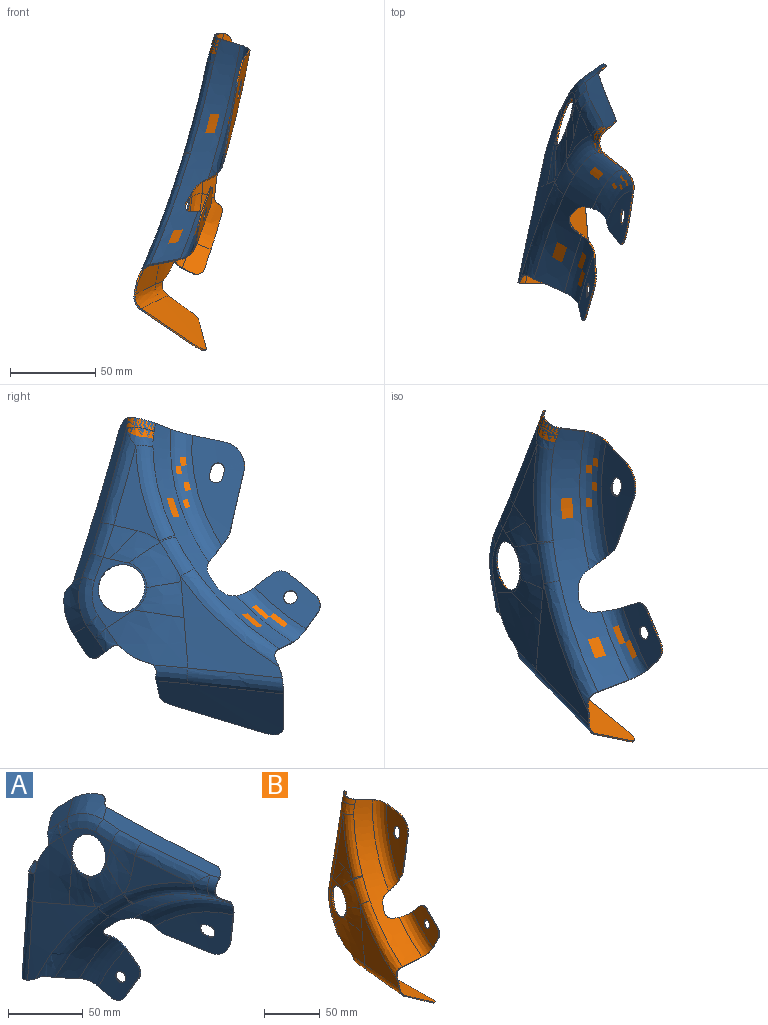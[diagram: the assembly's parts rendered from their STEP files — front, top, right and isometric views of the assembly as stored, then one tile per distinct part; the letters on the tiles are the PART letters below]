
ASSEMBLY  parts=2 mates=1
PART A: 121 faces, bbox 84.7x186.1x163.1 mm
  f0: bspline ~4.51x4.27mm, area 4.7mm2, adj f2,f57,f77,f82,f83
  f1: bspline ~11.83x11.52mm, area 10.9mm2, adj f3,f56,f78,f82
  f2: bspline ~3.38x2.32mm, area 2.6mm2, adj f0,f4,f57,f83
  f3: bspline ~22.43x11.8mm, area 19.2mm2, adj f1,f5,f49,f82,f113
  f4: bspline ~2.05x1.48mm, area 1.2mm2, adj f2,f6,f61,f83,f112,f118
  f5: bspline ~5.86x3.05mm, area 5.2mm2, adj f3,f7,f49,f113
  f6: bspline ~2.83x1.75mm, area 1.9mm2, adj f4,f8,f52,f118
  f7: bspline ~4.5x3mm, area 4.1mm2, adj f5,f9,f49,f109,f113
  f8: bspline ~19.93x6.73mm, area 15.8mm2, adj f6,f10,f52,f118
  f9: cylinder r=4.15mm len=0.84mm, axis (-0.47,-0.12,0.88), area 0.6mm2, adj f7,f11,f58,f109
  f10: bspline ~2.42x1.52mm, area 1.6mm2, adj f8,f12,f52,f118
  f11: bspline ~101.82x11.93mm, area 74.4mm2, adj f9,f13,f58,f109
  f12: bspline ~2.08x1.43mm, area 1.6mm2, adj f10,f14,f63,f111,f118
  f13: cylinder r=8mm len=8.65mm, axis (-0.48,-0.1,0.87), area 9.8mm2, adj f11,f15,f58,f67,f101,f109
  f14: bspline ~3.82x1.87mm, area 3mm2, adj f12,f16,f62,f86,f111
  f15: bspline ~16.48x5.32mm, area 14mm2, adj f13,f17,f67,f99,f101
  f16: bspline ~4.98x4.35mm, area 4.3mm2, adj f14,f18,f62,f86,f103
  f17: bspline ~12.23x10.39mm, area 12mm2, adj f15,f19,f73,f96,f99
  f18: plane 13.2x9.11mm, normal (0.22,0.13,0.97), area 12.7mm2, adj f16,f20,f71,f103
  f19: bspline ~14.72x6.4mm, area 12mm2, adj f17,f21,f76,f96
  f20: cylinder r=8mm len=6.82mm, axis (0.55,-0.84,-0.01), area 7.7mm2, adj f18,f22,f71,f103
  f21: bspline ~21.69x4.2mm, area 15.9mm2, adj f19,f23,f90,f91,f96
  f22: bspline ~71.44x6.29mm, area 47.9mm2, adj f20,f24,f71,f103
  f23: cylinder r=15mm len=14.9mm, axis (-0.98,-0.15,0.15), area 18.5mm2, adj f21,f25,f90,f91
  f24: cylinder r=8mm len=8.77mm, axis (0.55,-0.84,-0.02), area 11.4mm2, adj f22,f26,f71,f103
  f25: bspline ~42.95x8.43mm, area 29mm2, adj f23,f27,f90,f91
  f26: bspline ~34.29x23.06mm, area 29.6mm2, adj f24,f28,f71,f103
  f27: cylinder r=15mm len=6.26mm, axis (0.97,0.18,-0.15), area 5.1mm2, adj f25,f29,f90,f91
  f28: bspline ~9.53x4.9mm, area 8.2mm2, adj f26,f30,f70,f85,f103,f104
  f29: bspline ~4.56x2.11mm, area 3.2mm2, adj f27,f31,f90,f91,f96
  f30: bspline ~10.76x6.88mm, area 8.9mm2, adj f28,f32,f60,f69,f85,f105
  f31: bspline ~12.68x9.82mm, area 12.7mm2, adj f29,f33,f76,f96
  f32: bspline ~8.56x6.05mm, area 7.2mm2, adj f30,f34,f69,f105
  f33: bspline ~1.76x1.34mm, area 1mm2, adj f31,f35,f73,f96,f99
  f34: bspline ~2.48x1.69mm, area 1.4mm2, adj f32,f36,f69,f105
  f35: bspline ~10.16x9mm, area 10.3mm2, adj f33,f37,f73,f99
  f36: bspline ~21.82x8.6mm, area 15.9mm2, adj f34,f38,f73,f99
  f37: bspline ~5.6x5.48mm, area 5.1mm2, adj f35,f39,f73,f99
  f38: bspline ~11.21x9.99mm, area 12.1mm2, adj f36,f40,f75,f97
  f39: cylinder r=8mm len=10.98mm, axis (0.42,0.81,0.41), area 9.7mm2, adj f37,f41,f73,f99
  f40: plane 11.31x5.1mm, normal (-0.22,0.35,-0.91), area 9.3mm2, adj f38,f42,f81,f94
  f41: bspline ~4.39x3.12mm, area 3.2mm2, adj f39,f43,f73,f97,f99
  f42: cylinder r=8mm len=10.21mm, axis (0.97,0.19,-0.15), area 9.8mm2, adj f40,f44,f81,f94
  f43: bspline ~10.73x8.51mm, area 12mm2, adj f41,f45,f75,f97
  f44: bspline ~20.44x10.24mm, area 15.5mm2, adj f42,f46,f81,f94
  f45: bspline ~11.7x9.66mm, area 10.5mm2, adj f43,f46,f81,f94,f97
  f46: cylinder r=8mm len=10.29mm, axis (0.97,0.19,-0.15), area 9mm2, adj f44,f45,f81,f94
  f47: bspline ~30.17x15.79mm, area 269.7mm2, adj f48,f49,f50,f87
  f48: bspline ~13.36x11.37mm, area 93.8mm2, adj f47,f56,f57,f87
  f49: offset ~35.78x24.12mm, area 422.5mm2, adj f3,f5,f7,f47,f56,f58
  f50: bspline ~17.44x10.4mm, area 150.5mm2, adj f47,f58,f59,f87
  f51: bspline ~33.42x24.83mm, area 415.9mm2, adj f52,f55,f60,f87
  f52: bspline ~71.83x44.24mm, area 1192.4mm2, adj f6,f8,f10,f51,f57,f60,f61,f62
  f53: bspline ~26.4x21.82mm, area 186.9mm2, adj f54,f59,f64,f87
  f54: bspline ~29.44x21.67mm, area 278.1mm2, adj f53,f55,f64,f65,f87
  f55: bspline ~35.9x30.81mm, area 456mm2, adj f51,f54,f60,f66,f87
  f56: offset ~29.78x24.98mm, area 264.2mm2, adj f1,f48,f49,f57,f77,f78
  f57: bspline ~15.07x13.37mm, area 111.7mm2, adj f0,f2,f48,f52,f56,f61
  f58: offset ~121.86x43.87mm, area 882.1mm2, adj f9,f11,f13,f49,f50,f59,f67,f68
  f59: bspline ~20.06x9.5mm, area 201.2mm2, adj f50,f53,f58,f68
  f60: offset ~113.62x84.25mm, area 1455.9mm2, adj f30,f51,f52,f55,f69,f70
  f61: bspline ~1.94x1.77mm, area 0.7mm2, adj f4,f52,f57
  f62: bspline ~24.4x12.72mm, area 203.5mm2, adj f14,f16,f52,f63,f70,f71
  f63: bspline ~1.87x1.56mm, area 0.8mm2, adj f12,f52,f62
  f64: offset ~79.17x55.12mm, area 636mm2, adj f53,f54,f68,f72
  f65: bspline ~8.76x5.67mm, area 9.3mm2, adj f54,f66,f72,f73
  f66: bspline ~23.49x22.04mm, area 253mm2, adj f55,f65,f69,f73
  f67: bspline ~16.86x8.64mm, area 117.1mm2, adj f13,f15,f58,f73,f74
  f68: bspline ~58.01x14.08mm, area 548.5mm2, adj f58,f59,f64,f74
  f69: bspline ~72.3x44.62mm, area 847.3mm2, adj f30,f32,f34,f60,f66,f73
  f70: bspline ~58.13x16.25mm, area 601.8mm2, adj f28,f60,f62,f71
  f71: offset ~105.83x55.3mm, area 2491.8mm2, adj f18,f20,f22,f24,f26,f62,f70
  f72: bspline ~53.23x34.4mm, area 649.6mm2, adj f64,f65,f73,f74
  f73: bspline ~122.05x120.09mm, area 2720.6mm2, adj f17,f33,f35,f36,f37,f39,f41,f65
  f74: bspline ~17.71x11.19mm, area 163.2mm2, adj f67,f68,f72,f73
  f75: bspline ~44.63x28.08mm, area 614.5mm2, adj f38,f43,f73,f94
  f76: bspline ~72.37x48.53mm, area 1115.2mm2, adj f19,f31,f73,f91
  f77: bspline ~7.92x5.08mm, area 6.7mm2, adj f0,f56,f78,f82
  f78: cylinder r=8mm len=8.06mm, axis (-0.64,0.41,0.64), area 8.8mm2, adj f1,f56,f77,f82
  f79: cylinder r=4mm len=8.03mm, axis (-0.97,-0.2,0.15), area 20.1mm2, adj f81,f94
  f80: plane 4.08x1.43mm, normal (0.15,0,0.99), area 3.2mm2, adj f89,f90,f91,f92
  f81: offset ~52.95x40.69mm, area 654.1mm2, adj f40,f42,f44,f45,f46,f79,f97
  f82: offset ~31.38x26.58mm, area 277.1mm2, adj f0,f1,f3,f77,f78,f83,f113,f120
  f83: offset ~16.74x15.04mm, area 105.6mm2, adj f0,f2,f4,f82,f112,f118,f120
  f84: offset ~39.08x27.41mm, area 414.1mm2, adj f85,f95,f114,f118
  f85: offset ~115.22x85.85mm, area 1442.4mm2, adj f28,f30,f84,f104,f105,f114,f118
  f86: offset ~25.92x15.07mm, area 186.2mm2, adj f14,f16,f103,f104,f111,f118
  f87: plane 40.34x31.56mm, normal (-0.94,-0.09,0.32), area 338.4mm2, adj f47,f48,f50,f51,f52,f53,f54,f55
  f88: plane 4.08x1.44mm, normal (-0.15,0,-0.99), area 3.2mm2, adj f89,f90,f91,f92
  f89: cylinder r=4mm len=8.03mm, axis (-0.98,-0.16,0.15), area 10.1mm2, adj f80,f88,f90,f91
  f90: offset ~76.33x47.13mm, area 1258.8mm2, adj f21,f23,f25,f27,f29,f80,f88,f89
  f91: offset ~77.93x48.73mm, area 1258mm2, adj f21,f23,f25,f27,f29,f76,f80,f88
  f92: cylinder r=4mm len=8.03mm, axis (-0.98,-0.16,0.15), area 10.1mm2, adj f80,f88,f90,f91
  f93: cylinder r=14.3mm len=28.56mm, axis (0.94,0.09,-0.32), area 71.9mm2, adj f87,f95
  f94: offset ~54.55x42.29mm, area 653.6mm2, adj f40,f42,f44,f45,f46,f75,f79
  f95: plane 40.34x31.53mm, normal (0.94,0.09,-0.32), area 338.5mm2, adj f84,f93,f114,f115,f116,f117,f118,f119
  f96: bspline ~73.35x49.72mm, area 1186.2mm2, adj f17,f19,f21,f29,f31,f33,f90,f99
  f97: bspline ~45.42x28.67mm, area 649.9mm2, adj f38,f41,f43,f45,f81,f99
  f98: bspline ~16.45x11.15mm, area 149.3mm2, adj f99,f100,f101,f102
  f99: offset ~132.41x129.58mm, area 2733.7mm2, adj f15,f17,f33,f35,f36,f37,f39,f41
  f100: bspline ~53.62x33.87mm, area 599.4mm2, adj f98,f99,f107,f108
  f101: bspline ~15.45x8.29mm, area 108mm2, adj f13,f15,f98,f99,f109
  f102: offset ~59.61x15.66mm, area 514mm2, adj f98,f108,f109,f110
  f103: offset ~107.43x56.9mm, area 2539mm2, adj f16,f18,f20,f22,f24,f26,f28,f86
  f104: offset ~59.64x17.63mm, area 551mm2, adj f28,f85,f86,f103
  f105: bspline ~71.67x44.02mm, area 780.3mm2, adj f30,f32,f34,f85,f99,f106
  f106: bspline ~22.82x21.54mm, area 233.3mm2, adj f99,f105,f107,f114
  f107: bspline ~8.1x5.27mm, area 8.6mm2, adj f99,f100,f106,f115
  f108: offset ~80.77x56.72mm, area 635.9mm2, adj f100,f102,f115,f116
  f109: offset ~123.44x45.47mm, area 882.5mm2, adj f7,f9,f11,f13,f101,f102,f110,f113
  f110: offset ~21.46x11.03mm, area 188.8mm2, adj f102,f109,f116,f117
  f111: offset ~3.46x3.16mm, area 0.7mm2, adj f12,f14,f86,f118
  f112: offset ~3.53x3.37mm, area 0.7mm2, adj f4,f83,f118
  f113: offset ~37.38x25.71mm, area 415.6mm2, adj f3,f5,f7,f82,f109,f119
  f114: offset ~39.37x34.5mm, area 451.8mm2, adj f84,f85,f95,f106,f115
  f115: offset ~33.62x25.23mm, area 277.9mm2, adj f95,f107,f108,f114,f116
  f116: offset ~28.22x24.23mm, area 187.1mm2, adj f95,f108,f110,f115
  f117: offset ~18.82x12.68mm, area 141.8mm2, adj f95,f109,f110,f119
  f118: offset ~75.43x47.94mm, area 1189.7mm2, adj f4,f6,f8,f10,f12,f83,f84,f85
  f119: offset ~33.21x17.53mm, area 253mm2, adj f95,f113,f117,f120
  f120: offset ~14.96x12.97mm, area 88.8mm2, adj f82,f83,f95,f119
PART B: 121 faces, bbox 84.7x163.1x186.1 mm
  f0: bspline ~4.51x4.27mm, area 4.7mm2, adj f2,f57,f77,f82,f83
  f1: bspline ~11.83x11.52mm, area 10.9mm2, adj f3,f56,f78,f82
  f2: bspline ~3.38x2.32mm, area 2.6mm2, adj f0,f4,f57,f83
  f3: bspline ~22.43x11.8mm, area 19.2mm2, adj f1,f5,f49,f82,f113
  f4: bspline ~2.05x1.48mm, area 1.2mm2, adj f2,f6,f61,f83,f112,f118
  f5: bspline ~5.86x3.05mm, area 5.2mm2, adj f3,f7,f49,f113
  f6: bspline ~2.83x1.75mm, area 1.9mm2, adj f4,f8,f52,f118
  f7: bspline ~4.5x3mm, area 4.1mm2, adj f5,f9,f49,f109,f113
  f8: bspline ~19.93x6.73mm, area 15.8mm2, adj f6,f10,f52,f118
  f9: cylinder r=4.15mm len=0.84mm, axis (-0.47,0.88,0.12), area 0.6mm2, adj f7,f11,f58,f109
  f10: bspline ~2.42x1.52mm, area 1.6mm2, adj f8,f12,f52,f118
  f11: bspline ~101.82x11.93mm, area 74.4mm2, adj f9,f13,f58,f109
  f12: bspline ~2.08x1.43mm, area 1.6mm2, adj f10,f14,f63,f111,f118
  f13: cylinder r=8mm len=8.65mm, axis (-0.48,0.87,0.1), area 9.8mm2, adj f11,f15,f58,f67,f101,f109
  f14: bspline ~3.82x1.87mm, area 3mm2, adj f12,f16,f62,f86,f111
  f15: bspline ~16.48x5.32mm, area 14mm2, adj f13,f17,f67,f99,f101
  f16: bspline ~4.98x4.35mm, area 4.3mm2, adj f14,f18,f62,f86,f103
  f17: bspline ~12.23x10.39mm, area 12mm2, adj f15,f19,f73,f96,f99
  f18: plane 13.2x9.11mm, normal (0.22,0.97,-0.13), area 12.7mm2, adj f16,f20,f71,f103
  f19: bspline ~14.72x6.4mm, area 12mm2, adj f17,f21,f76,f96
  f20: cylinder r=8mm len=6.82mm, axis (0.55,-0.01,0.84), area 7.7mm2, adj f18,f22,f71,f103
  f21: bspline ~21.69x4.2mm, area 15.9mm2, adj f19,f23,f90,f91,f96
  f22: bspline ~71.44x6.29mm, area 47.9mm2, adj f20,f24,f71,f103
  f23: cylinder r=15mm len=14.9mm, axis (-0.98,0.15,0.15), area 18.5mm2, adj f21,f25,f90,f91
  f24: cylinder r=8mm len=8.77mm, axis (0.55,-0.02,0.84), area 11.4mm2, adj f22,f26,f71,f103
  f25: bspline ~42.95x8.43mm, area 29mm2, adj f23,f27,f90,f91
  f26: bspline ~34.29x23.06mm, area 29.6mm2, adj f24,f28,f71,f103
  f27: cylinder r=15mm len=6.26mm, axis (0.97,-0.15,-0.18), area 5.1mm2, adj f25,f29,f90,f91
  f28: bspline ~9.53x4.9mm, area 8.2mm2, adj f26,f30,f70,f85,f103,f104
  f29: bspline ~4.56x2.11mm, area 3.2mm2, adj f27,f31,f90,f91,f96
  f30: bspline ~10.76x6.88mm, area 8.9mm2, adj f28,f32,f60,f69,f85,f105
  f31: bspline ~12.68x9.82mm, area 12.7mm2, adj f29,f33,f76,f96
  f32: bspline ~8.56x6.05mm, area 7.2mm2, adj f30,f34,f69,f105
  f33: bspline ~1.76x1.34mm, area 1mm2, adj f31,f35,f73,f96,f99
  f34: bspline ~2.48x1.69mm, area 1.4mm2, adj f32,f36,f69,f105
  f35: bspline ~10.16x9mm, area 10.3mm2, adj f33,f37,f73,f99
  f36: bspline ~21.82x8.6mm, area 15.9mm2, adj f34,f38,f73,f99
  f37: bspline ~5.6x5.48mm, area 5.1mm2, adj f35,f39,f73,f99
  f38: bspline ~11.21x9.99mm, area 12.1mm2, adj f36,f40,f75,f97
  f39: cylinder r=8mm len=10.98mm, axis (0.42,0.41,-0.81), area 9.7mm2, adj f37,f41,f73,f99
  f40: plane 11.31x5.1mm, normal (-0.22,-0.91,-0.35), area 9.3mm2, adj f38,f42,f81,f94
  f41: bspline ~4.39x3.12mm, area 3.2mm2, adj f39,f43,f73,f97,f99
  f42: cylinder r=8mm len=10.21mm, axis (0.97,-0.15,-0.19), area 9.8mm2, adj f40,f44,f81,f94
  f43: bspline ~10.73x8.51mm, area 12mm2, adj f41,f45,f75,f97
  f44: bspline ~20.44x10.24mm, area 15.5mm2, adj f42,f46,f81,f94
  f45: bspline ~11.7x9.66mm, area 10.5mm2, adj f43,f46,f81,f94,f97
  f46: cylinder r=8mm len=10.29mm, axis (0.97,-0.15,-0.19), area 9mm2, adj f44,f45,f81,f94
  f47: bspline ~30.17x15.79mm, area 269.7mm2, adj f48,f49,f50,f87
  f48: bspline ~13.36x11.37mm, area 93.8mm2, adj f47,f56,f57,f87
  f49: offset ~35.78x24.12mm, area 422.5mm2, adj f3,f5,f7,f47,f56,f58
  f50: bspline ~17.44x10.4mm, area 150.5mm2, adj f47,f58,f59,f87
  f51: bspline ~33.42x24.83mm, area 415.9mm2, adj f52,f55,f60,f87
  f52: bspline ~71.83x44.24mm, area 1192.4mm2, adj f6,f8,f10,f51,f57,f60,f61,f62
  f53: bspline ~26.4x21.82mm, area 186.9mm2, adj f54,f59,f64,f87
  f54: bspline ~29.44x21.67mm, area 278.1mm2, adj f53,f55,f64,f65,f87
  f55: bspline ~35.9x30.81mm, area 456mm2, adj f51,f54,f60,f66,f87
  f56: offset ~29.78x24.98mm, area 264.2mm2, adj f1,f48,f49,f57,f77,f78
  f57: bspline ~15.07x13.37mm, area 111.7mm2, adj f0,f2,f48,f52,f56,f61
  f58: offset ~121.86x43.87mm, area 882.1mm2, adj f9,f11,f13,f49,f50,f59,f67,f68
  f59: bspline ~20.06x9.5mm, area 201.2mm2, adj f50,f53,f58,f68
  f60: offset ~113.62x84.25mm, area 1455.9mm2, adj f30,f51,f52,f55,f69,f70
  f61: bspline ~1.94x1.77mm, area 0.7mm2, adj f4,f52,f57
  f62: bspline ~24.4x12.72mm, area 203.5mm2, adj f14,f16,f52,f63,f70,f71
  f63: bspline ~1.87x1.56mm, area 0.8mm2, adj f12,f52,f62
  f64: offset ~79.17x55.12mm, area 636mm2, adj f53,f54,f68,f72
  f65: bspline ~8.76x5.67mm, area 9.3mm2, adj f54,f66,f72,f73
  f66: bspline ~23.49x22.04mm, area 253mm2, adj f55,f65,f69,f73
  f67: bspline ~16.86x8.64mm, area 117.1mm2, adj f13,f15,f58,f73,f74
  f68: bspline ~58.01x14.08mm, area 548.5mm2, adj f58,f59,f64,f74
  f69: bspline ~72.3x44.62mm, area 847.3mm2, adj f30,f32,f34,f60,f66,f73
  f70: bspline ~58.13x16.25mm, area 601.8mm2, adj f28,f60,f62,f71
  f71: offset ~105.83x55.3mm, area 2491.8mm2, adj f18,f20,f22,f24,f26,f62,f70
  f72: bspline ~53.23x34.4mm, area 649.6mm2, adj f64,f65,f73,f74
  f73: bspline ~122.05x120.09mm, area 2720.6mm2, adj f17,f33,f35,f36,f37,f39,f41,f65
  f74: bspline ~17.71x11.19mm, area 163.2mm2, adj f67,f68,f72,f73
  f75: bspline ~44.63x28.08mm, area 614.5mm2, adj f38,f43,f73,f94
  f76: bspline ~72.37x48.53mm, area 1115.2mm2, adj f19,f31,f73,f91
  f77: bspline ~7.92x5.08mm, area 6.7mm2, adj f0,f56,f78,f82
  f78: cylinder r=8mm len=8.06mm, axis (-0.64,0.64,-0.41), area 8.8mm2, adj f1,f56,f77,f82
  f79: cylinder r=4mm len=8.03mm, axis (-0.97,0.15,0.2), area 20.1mm2, adj f81,f94
  f80: plane 4.08x1.43mm, normal (0.15,0.99,0), area 3.2mm2, adj f89,f90,f91,f92
  f81: offset ~52.95x40.69mm, area 654.1mm2, adj f40,f42,f44,f45,f46,f79,f97
  f82: offset ~31.38x26.58mm, area 277.1mm2, adj f0,f1,f3,f77,f78,f83,f113,f120
  f83: offset ~16.74x15.04mm, area 105.6mm2, adj f0,f2,f4,f82,f112,f118,f120
  f84: offset ~39.08x27.41mm, area 414.1mm2, adj f85,f95,f114,f118
  f85: offset ~115.22x85.85mm, area 1442.4mm2, adj f28,f30,f84,f104,f105,f114,f118
  f86: offset ~25.92x15.07mm, area 186.2mm2, adj f14,f16,f103,f104,f111,f118
  f87: plane 40.34x31.56mm, normal (-0.94,0.32,0.09), area 338.4mm2, adj f47,f48,f50,f51,f52,f53,f54,f55
  f88: plane 4.08x1.44mm, normal (-0.15,-0.99,0), area 3.2mm2, adj f89,f90,f91,f92
  f89: cylinder r=4mm len=8.03mm, axis (-0.98,0.15,0.16), area 10.1mm2, adj f80,f88,f90,f91
  f90: offset ~76.33x47.13mm, area 1258.8mm2, adj f21,f23,f25,f27,f29,f80,f88,f89
  f91: offset ~77.93x48.73mm, area 1258mm2, adj f21,f23,f25,f27,f29,f76,f80,f88
  f92: cylinder r=4mm len=8.03mm, axis (-0.98,0.15,0.16), area 10.1mm2, adj f80,f88,f90,f91
  f93: cylinder r=14.3mm len=28.56mm, axis (0.94,-0.32,-0.09), area 71.9mm2, adj f87,f95
  f94: offset ~54.55x42.29mm, area 653.6mm2, adj f40,f42,f44,f45,f46,f75,f79
  f95: plane 40.34x31.53mm, normal (0.94,-0.32,-0.09), area 338.5mm2, adj f84,f93,f114,f115,f116,f117,f118,f119
  f96: bspline ~73.35x49.72mm, area 1186.2mm2, adj f17,f19,f21,f29,f31,f33,f90,f99
  f97: bspline ~45.42x28.67mm, area 649.9mm2, adj f38,f41,f43,f45,f81,f99
  f98: bspline ~16.45x11.15mm, area 149.3mm2, adj f99,f100,f101,f102
  f99: offset ~132.41x129.58mm, area 2733.7mm2, adj f15,f17,f33,f35,f36,f37,f39,f41
  f100: bspline ~53.62x33.87mm, area 599.4mm2, adj f98,f99,f107,f108
  f101: bspline ~15.45x8.29mm, area 108mm2, adj f13,f15,f98,f99,f109
  f102: offset ~59.61x15.66mm, area 514mm2, adj f98,f108,f109,f110
  f103: offset ~107.43x56.9mm, area 2539mm2, adj f16,f18,f20,f22,f24,f26,f28,f86
  f104: offset ~59.64x17.63mm, area 551mm2, adj f28,f85,f86,f103
  f105: bspline ~71.67x44.02mm, area 780.3mm2, adj f30,f32,f34,f85,f99,f106
  f106: bspline ~22.82x21.54mm, area 233.3mm2, adj f99,f105,f107,f114
  f107: bspline ~8.1x5.27mm, area 8.6mm2, adj f99,f100,f106,f115
  f108: offset ~80.77x56.72mm, area 635.9mm2, adj f100,f102,f115,f116
  f109: offset ~123.44x45.47mm, area 882.5mm2, adj f7,f9,f11,f13,f101,f102,f110,f113
  f110: offset ~21.46x11.03mm, area 188.8mm2, adj f102,f109,f116,f117
  f111: offset ~3.46x3.16mm, area 0.7mm2, adj f12,f14,f86,f118
  f112: offset ~3.53x3.37mm, area 0.7mm2, adj f4,f83,f118
  f113: offset ~37.38x25.71mm, area 415.6mm2, adj f3,f5,f7,f82,f109,f119
  f114: offset ~39.37x34.5mm, area 451.8mm2, adj f84,f85,f95,f106,f115
  f115: offset ~33.62x25.23mm, area 277.9mm2, adj f95,f107,f108,f114,f116
  f116: offset ~28.22x24.23mm, area 187.1mm2, adj f95,f108,f110,f115
  f117: offset ~18.82x12.68mm, area 141.8mm2, adj f95,f109,f110,f119
  f118: offset ~75.43x47.94mm, area 1189.7mm2, adj f4,f6,f8,f10,f12,f83,f84,f85
  f119: offset ~33.21x17.53mm, area 253mm2, adj f95,f113,f117,f120
  f120: offset ~14.96x12.97mm, area 88.8mm2, adj f82,f83,f95,f119
PLACE A rot(axis=(-1,0,0),77.1deg) t=(54.25,996.14,256.79)mm
PLACE B rot(axis=(1,0,0),12.9deg) t=(54.25,996.14,256.79)mm
MATE fastened B.f93 <-> A.f93  axis (-0.94,0.3,0.16) through (3535.35,822.59,-324.88)mm
